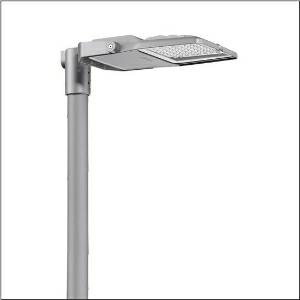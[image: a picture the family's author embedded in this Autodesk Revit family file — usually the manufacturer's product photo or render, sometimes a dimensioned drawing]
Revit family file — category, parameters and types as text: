
# Revit family: floodlight_fl_21_mini___pl43_5xa7776d2a3a_6ee6
name_source: partatom
category: Lighting Fixtures
units: mm (PartAtom-declared; Revit-internal decimal feet)

## family parameters
Cut with Voids When Loaded = No
Host = Face
Light Source = No
Part Type = Normal
Room Calculation Point = No
Round Connector Dimension = Use Diameter
Shared = No

## types (1)
- --- (1 x LED, 18300 lm, 142.9 W, 3000K)
    Apparent Load = 143 VA
    CIE Flux Codes = 27 78 99 100 100
    Color Rendering = 70
    Color Temperature = 3000K
    Default Elevation = 1800 mm
    Description = Floodlight FL 21 mini, floodlight, primary light control with lens, of PMMA, primary optical cover: protective disc, of toughened safety glass, transparent, light distribution: PL43, light emission: direct distribution, installation type: surface-mounted, LED, High Power LED, rated luminous flux: 18.300lm, luminous efficacy: 128lm/W, light colour: 730, colour temperature: 3000K, control gear: Smart Interface (Zhaga), control: flexible luminous flux parameterisation, time-dependent luminous flux control, constant luminous flux control, overheat protection, pre-setting: logarithmic dimming characteristic, with terminal, 6-pole, mains connection: 220..240V, AC, 50/60Hz, start of lifetime: 143W, end of service life: 151W, reduction: 63W, luminaire housing, of diecast aluminium, powder-coated, Siteco® metallic grey (DB 702S), corrosivity category C5 mid according to DIN EN ISO 12944, suitable for swimming pools, chlorine-resistant, sealing non-destructively replaceable, please order mast flange separately, mast bracket, of steel, galvanised, powder-coated, Siteco® metallic grey (DB 702S), Smart Interface below and above, protection rating (complete): IP66, insulation class (complete): insulation class II (safety insulation), certification: CE, ENEC, VDE, protection symbol: D, impact resistance: IK08, permissible operating ambient temperature: -40..+40°C, permissible operating ambient temperature for outdoor applications: -40..+50°C, standard: DIN EN 12944, LABS conformity tested according to VDMA 24364:2018-05, packaging unit: 1 piece

Light Distribution: PL43
    Height = 70 mm
    Lamp = 1 x LED
    Lamp Light Flux = 18300 lm
    Lamp Power = 142.9 W
    Lamp count = 1
    Length = 485 mm
    Luminous efficacy = 128 lm/W
    Manufacturer = Siteco
    ModVariant = No
    Model = 5XA7776D2A3A
    Number of Poles = 1
    OnlyDefault = Yes
    Power Factor = 1
    Product Name = Floodlight FL 21 mini | PL43
    Product group = floodlight | pylon annexe
    ProductGroupID = 6201
    Protection Class = Protection class II
    Protection Degree = IP 66
    RLX_Detail_Level = 1
    RLX_Emergency_Light_Flux = 0 lm
    RLX_Emergency_Type = 0
    RLX_Emergency_Type_DB = No
    RlxData = <blob elided: 101233 chars, md5=dcee4a0b>
    Socket = socket
    Standby Power = 0 W
    System Light Flux = 18300 lm
    System Power = 143 W
    Type Comments = factory setting: luminous flux: 100 % | dim-lin: 254 | 730 mA
    Type Image = l_1007125.jpg
    URL = http://relux.com
    VarID = @adj_182393
    Voltage = 0 V
    Weight = 0.00 kg
    Width = 337 mm

## geometry (parser evidence)
native form markers: Blend x4, Sweep x11
no freeform markers — native parametric forms only
